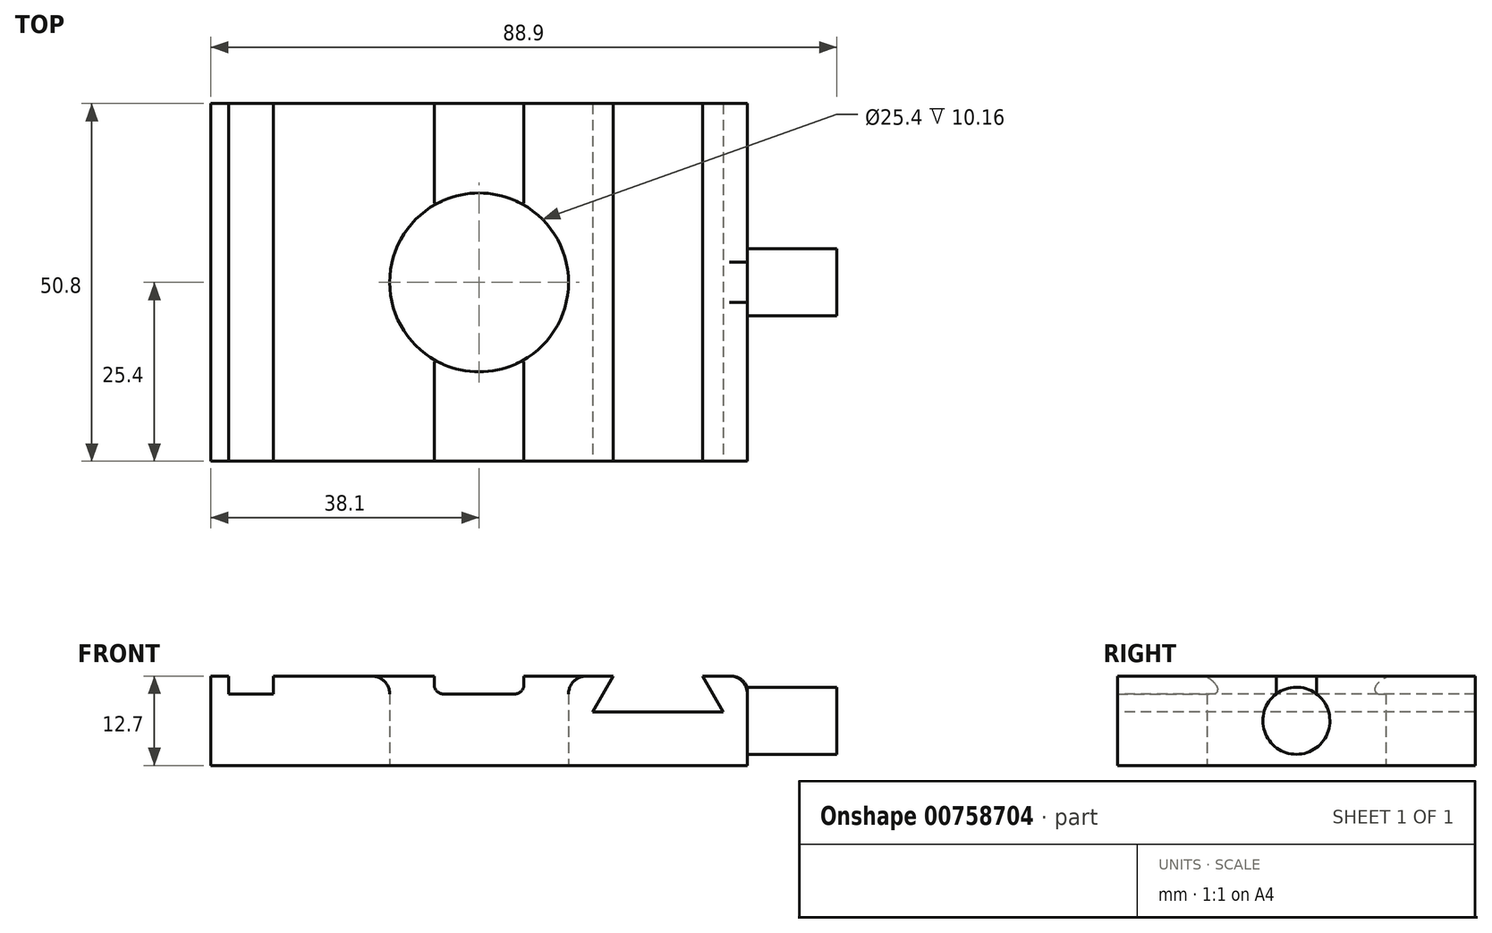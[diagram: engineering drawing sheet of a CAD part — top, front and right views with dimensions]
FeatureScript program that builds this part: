
annotation { "Feature Type Name" : "Feature", "Feature Type Description" : "" }
export const myFeature = defineFeature(function(context is Context, id is Id, definition is map)
    precondition{}
    {
        {
            var Q0;
            Q0=qCreatedBy(makeId("Top.planeOp"),FACE);
            var sketch = newSketch(context, id + "F0", { "sketchPlane" : qUnion([Q0])});
            skLineSegment(sketch, "E0.bottom", {"start": v(38.1, 25.4) * mm, "end": v(-38.1, 25.4) * mm});
            skLineSegment(sketch, "E0.top", {"start": v(38.1, -25.4) * mm, "end": v(-38.1, -25.4) * mm});
            skLineSegment(sketch, "E0.left", {"start": v(38.1, 25.4) * mm, "end": v(38.1, -25.4) * mm});
            skLineSegment(sketch, "E0.right", {"start": v(-38.1, 25.4) * mm, "end": v(-38.1, -25.4) * mm});
            skPoint(sketch, "E0.middle", {"position": v(0, 0) * mm});
            skCircle(sketch, "E1", {"center": v(0, 0) * mm, "radius": 12.7 * mm});
            skSolve(sketch);
        }
        {
            var Q0;
            Q0=makeQuery(id+"F0.imprint","IMPRINT",FACE,{"disambiguationData":[TD([[makeQuery(id+"F0.imprint","IMPRINT",EDGE,{"derivedFrom":sQuery(id+"F0.wireOp",EDGE,"E0.bottom")}),1.0]])]});
            extrude(context, id + "F1", {"entities" : qUnion([Q0]), "depth" : 12.7 * mm, "offsetDistance" : 25.4 * mm});
        }
        {
            var Q0;
            Q0=makeQuery(id+"F1.opExtrude","CAP_FACE",FACE,{"disambiguationData":[OSD([sQuery(id+"F0.wireOp",EDGE,"E0.bottom"),sQuery(id+"F0.wireOp",EDGE,"E0.top"),sQuery(id+"F0.wireOp",EDGE,"E0.left"),sQuery(id+"F0.wireOp",EDGE,"E0.right"),sQuery(id+"F0.wireOp",EDGE,"E1")])],"isStart":false});
            var sketch = newSketch(context, id + "F2", { "sketchPlane" : qUnion([Q0])});
            skLineSegment(sketch, "E2.bottom", {"start": v(-35.56, 25.4) * mm, "end": v(-29.2, 25.4) * mm});
            skLineSegment(sketch, "E2.top", {"start": v(-35.56, -25.4) * mm, "end": v(-29.2, -25.4) * mm});
            skLineSegment(sketch, "E2.left", {"start": v(-35.56, 25.4) * mm, "end": v(-35.56, -25.4) * mm});
            skLineSegment(sketch, "E2.right", {"start": v(-29.2, 25.4) * mm, "end": v(-29.2, -25.4) * mm});
            skLineSegment(sketch, "E3", {"start": v(-6.35, 25.4) * mm, "end": v(-6.35, -25.4) * mm});
            skLineSegment(sketch, "E4", {"start": v(-6.35, -25.4) * mm, "end": v(6.35, -25.4) * mm});
            skLineSegment(sketch, "E5", {"start": v(6.35, -25.4) * mm, "end": v(6.35, 25.4) * mm});
            skPoint(sketch, "E6", {"position": v(0, 0) * mm});
            skLineSegment(sketch, "E7", {"start": v(0, -25.4) * mm, "end": v(0, 25.4) * mm, "construction": true});
            skPoint(sketch, "E7.endSnap0", {"position": v(0, 25.4) * mm});
            skSolve(sketch);
        }
        {
            var Q0;
            Q0=makeQuery(id+"F2.imprint","IMPRINT",FACE,{"disambiguationData":[TD([[makeQuery(id+"F2.imprint","IMPRINT",EDGE,{"derivedFrom":sQuery(id+"F2.wireOp",EDGE,"E2.bottom")}),1.0]])]});
            var Q1;
            {var subQ0=sQuery(id+"F2.wireOp",EDGE,"E4");Q1=makeQuery(id+"F2.imprint","IMPRINT",FACE,{"disambiguationData":[TD([[makeQuery(id+"F2.imprint","IMPRINT",EDGE,{"derivedFrom":subQ0}),-1.0]])]});}
            var Q2;
            {var subQ0=sQuery(id+"F2.wireOp",EDGE,"E3");var subQ1=makeQuery(id+"F1.opExtrude","CAP_EDGE",EDGE,{"disambiguationData":[OSD([sQuery(id+"F0.wireOp",EDGE,"E0.bottom")])],"isStart":false});var subQ2=makeQuery(id+"F2.imprint","INTERSECT",VERTEX,{"derivedFrom":[subQ1,subQ0]});Q2=makeQuery(id+"F2.imprint","IMPRINT",FACE,{"disambiguationData":[TD([[makeQuery(id+"F2.imprint","IMPRINT",EDGE,{"disambiguationData":[TD([[subQ2,-1.0]])],"derivedFrom":subQ0}),1.0]])]});}
            extrude(context, id + "F3", {"entities" : qUnion([Q0, Q1, Q2]), "operationType" : NewBodyOperationType.REMOVE, "oppositeDirection" : true, "depth" : 2.54 * mm, "offsetDistance" : 25.4 * mm});
        }
        {
            var Q0;
            Q0=makeQuery(id+"F1.opExtrude","SWEPT_FACE",FACE,{"disambiguationData":[OSD([sQuery(id+"F0.wireOp",EDGE,"E0.top")])]});
            var sketch = newSketch(context, id + "F4", { "sketchPlane" : qUnion([Q0])});
            skLineSegment(sketch, "E8", {"start": v(19.05, 12.7) * mm, "end": v(16.12, 7.62) * mm});
            skLineSegment(sketch, "E9", {"start": v(16.12, 7.62) * mm, "end": v(34.68, 7.62) * mm});
            skLineSegment(sketch, "E10", {"start": v(34.68, 7.62) * mm, "end": v(31.75, 12.7) * mm});
            skLineSegment(sketch, "E11", {"start": v(31.75, 12.7) * mm, "end": v(19.05, 12.7) * mm});
            skLineSegment(sketch, "E12", {"start": v(25.4, 7.62) * mm, "end": v(25.4, 12.7) * mm, "construction": true});
            skSolve(sketch);
        }
        {
            var Q0;
            Q0=makeQuery(id+"F4.imprint","IMPRINT",FACE,{"disambiguationData":[TD([[makeQuery(id+"F4.imprint","IMPRINT",EDGE,{"derivedFrom":sQuery(id+"F4.wireOp",EDGE,"E8")}),1.0]])]});
            extrude(context, id + "F5", {"entities" : qUnion([Q0]), "operationType" : NewBodyOperationType.REMOVE, "endBound" : BoundingType.THROUGH_ALL, "oppositeDirection" : true, "depth" : 25.4 * mm, "offsetDistance" : 25.4 * mm});
        }
        {
            var Q0;
            Q0=makeQuery(id+"F1.opExtrude","SWEPT_FACE",FACE,{"disambiguationData":[OSD([sQuery(id+"F0.wireOp",EDGE,"E0.left")])]});
            var sketch = newSketch(context, id + "F6", { "sketchPlane" : qUnion([Q0])});
            skCircle(sketch, "E13", {"center": v(0, 6.35) * mm, "radius": 4.76 * mm});
            skPoint(sketch, "E13.centerSnap0", {"position": v(-25.4, 6.35) * mm});
            skPoint(sketch, "E13.centerSnap1", {"position": v(0, 12.7) * mm});
            skSolve(sketch);
        }
        {
            var Q0;
            Q0=makeQuery(id+"F6.imprint","IMPRINT",FACE,{"disambiguationData":[TD([[makeQuery(id+"F6.imprint","IMPRINT",EDGE,{"derivedFrom":sQuery(id+"F6.wireOp",EDGE,"E13")}),1.0]])]});
            extrude(context, id + "F7", {"entities" : qUnion([Q0]), "operationType" : NewBodyOperationType.ADD, "depth" : 12.7 * mm, "offsetDistance" : 25.4 * mm});
        }
        {
            var Q0;
            Q0=makeQuery(id+"F1.opExtrude","CAP_EDGE",EDGE,{"disambiguationData":[OSD([sQuery(id+"F0.wireOp",EDGE,"E0.left")])],"isStart":false});
            fillet(context, id + "F8", {"entities" : qUnion([Q0]), "radius" : 2.54 * mm, "tangentPropagation" : true, "allowEdgeOverflow" : false});
        }
        {
            var Q0;
            {var subQ0=sQuery(id+"F0.wireOp",EDGE,"E1");var subQ2=sQuery(id+"F0.wireOp",EDGE,"E0.bottom");var subQ3=sQuery(id+"F2.wireOp",EDGE,"E5");var subQ4=makeQuery(id+"F1.opExtrude","CAP_EDGE",EDGE,{"disambiguationData":[OSD([subQ0])],"isStart":false});Q0=makeQuery(id+"F3.boolean.opBoolean","SPLIT",EDGE,{"disambiguationData":[TD([makeQuery(id+"F3.opExtrude","SWEPT_FACE",FACE,{"disambiguationData":[OSD([subQ3]),TDD([makeQuery(id+"F2.imprint","IMPRINT",EDGE,{"disambiguationData":[TD([[makeQuery(id+"F2.imprint","INTERSECT",VERTEX,{"derivedFrom":[makeQuery(id+"F1.opExtrude","CAP_EDGE",EDGE,{"disambiguationData":[OSD([subQ2])],"isStart":false}),subQ3]}),1.0]])],"derivedFrom":subQ3})])]})])],"derivedFrom":subQ4});}
            var Q1;
            {var subQ0=sQuery(id+"F0.wireOp",EDGE,"E1");var subQ2=sQuery(id+"F0.wireOp",EDGE,"E0.bottom");var subQ3=sQuery(id+"F2.wireOp",EDGE,"E3");var subQ4=makeQuery(id+"F1.opExtrude","CAP_EDGE",EDGE,{"disambiguationData":[OSD([subQ0])],"isStart":false});Q1=makeQuery(id+"F3.boolean.opBoolean","SPLIT",EDGE,{"disambiguationData":[TD([makeQuery(id+"F3.opExtrude","SWEPT_FACE",FACE,{"disambiguationData":[OSD([subQ3]),TDD([makeQuery(id+"F2.imprint","IMPRINT",EDGE,{"disambiguationData":[TD([[makeQuery(id+"F2.imprint","INTERSECT",VERTEX,{"derivedFrom":[makeQuery(id+"F1.opExtrude","CAP_EDGE",EDGE,{"disambiguationData":[OSD([subQ2])],"isStart":false}),subQ3]}),-1.0]])],"derivedFrom":subQ3})])]})])],"derivedFrom":subQ4});}
            fillet(context, id + "F9", {"entities" : qUnion([Q0, Q1]), "radius" : 2.54 * mm, "tangentPropagation" : true, "allowEdgeOverflow" : false});
        }
        {
            var Q0;
            {var subQ0=sQuery(id+"F2.wireOp",EDGE,"E5");Q0=makeQuery(id+"F3.boolean.opBoolean","COPY",EDGE,{"derivedFrom":makeQuery(id+"F3.opExtrude","CAP_EDGE",EDGE,{"disambiguationData":[OSD([subQ0]),TDD([makeQuery(id+"F2.imprint","IMPRINT",EDGE,{"disambiguationData":[TD([[makeQuery(id+"F2.imprint","INTERSECT",VERTEX,{"derivedFrom":[makeQuery(id+"F1.opExtrude","CAP_EDGE",EDGE,{"disambiguationData":[OSD([sQuery(id+"F0.wireOp",EDGE,"E0.bottom")])],"isStart":false}),subQ0]}),1.0]])],"derivedFrom":subQ0})])],"isStart":false})});}
            var Q1;
            {var subQ0=sQuery(id+"F2.wireOp",EDGE,"E3");Q1=makeQuery(id+"F3.boolean.opBoolean","COPY",EDGE,{"derivedFrom":makeQuery(id+"F3.opExtrude","CAP_EDGE",EDGE,{"disambiguationData":[OSD([subQ0]),TDD([makeQuery(id+"F2.imprint","IMPRINT",EDGE,{"disambiguationData":[TD([[makeQuery(id+"F2.imprint","INTERSECT",VERTEX,{"derivedFrom":[makeQuery(id+"F1.opExtrude","CAP_EDGE",EDGE,{"disambiguationData":[OSD([sQuery(id+"F0.wireOp",EDGE,"E0.bottom")])],"isStart":false}),subQ0]}),-1.0]])],"derivedFrom":subQ0})])],"isStart":false})});}
            var Q2;
            {var subQ0=sQuery(id+"F2.wireOp",EDGE,"E3");Q2=makeQuery(id+"F3.boolean.opBoolean","COPY",EDGE,{"derivedFrom":makeQuery(id+"F3.opExtrude","CAP_EDGE",EDGE,{"disambiguationData":[OSD([subQ0]),TDD([makeQuery(id+"F2.imprint","IMPRINT",EDGE,{"disambiguationData":[TD([[makeQuery(id+"F2.imprint","INTERSECT",VERTEX,{"disambiguationData":[OD(1.0)],"derivedFrom":[makeQuery(id+"F1.opExtrude","CAP_EDGE",EDGE,{"disambiguationData":[OSD([sQuery(id+"F0.wireOp",EDGE,"E1")])],"isStart":false}),subQ0]}),-1.0]])],"derivedFrom":subQ0})])],"isStart":false})});}
            var Q3;
            {var subQ0=sQuery(id+"F2.wireOp",EDGE,"E5");Q3=makeQuery(id+"F3.boolean.opBoolean","COPY",EDGE,{"derivedFrom":makeQuery(id+"F3.opExtrude","CAP_EDGE",EDGE,{"disambiguationData":[OSD([subQ0]),TDD([makeQuery(id+"F2.imprint","IMPRINT",EDGE,{"disambiguationData":[TD([[makeQuery(id+"F2.imprint","INTERSECT",VERTEX,{"disambiguationData":[OD(0.0)],"derivedFrom":[makeQuery(id+"F1.opExtrude","CAP_EDGE",EDGE,{"disambiguationData":[OSD([sQuery(id+"F0.wireOp",EDGE,"E1")])],"isStart":false}),subQ0]}),1.0]])],"derivedFrom":subQ0})])],"isStart":false})});}
            fillet(context, id + "F10", {"entities" : qUnion([Q0, Q1, Q2, Q3]), "radius" : 1.27 * mm, "tangentPropagation" : true, "allowEdgeOverflow" : false});
        }
    });
